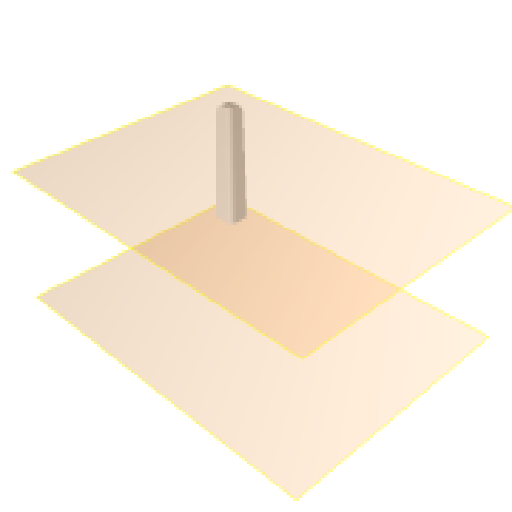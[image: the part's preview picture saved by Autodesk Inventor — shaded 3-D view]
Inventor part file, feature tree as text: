
AUTODESK INVENTOR PART (.ipt)
format: ipt  version: 2024.1 (Build 281209000, 209)  size: 171,008 bytes
history: native  units: mm
features: reference x4, sketch x3, plane x2, other x2, loft x1, extrude x1, fillet x1
ambient origin geometry x8: Origin, YZ Plane, XZ Plane, XY Plane, X Axis, Y Axis, Z Axis, Center Point
bodies: Body1 (feature_tree)
feature tree (14):
  plane  "Arbeitsebene1"
  sketch  "Skizze1"  dims[d0=10.0mm d1=2.0mm]
  plane  "Arbeitsebene2"
  loft  "Erhebung1"
  extrude  "Extrusion4"  TaperAngle=0.0deg  [1 undecoded]
  fillet  "Rundung1"  [1 undecoded]
  reference  "Referenz1"
  sketch  "Skizze4"  dims[d8=4.0mm d9=0.0mm d10=90.0deg d11=0.0mm d12=90.0deg]
  sketch  "Skizze5"  dims[d13=60.0mm d14=0.0mm d15=8.0mm d16=105.7mm]
  reference  "Referenz2"
  reference  "Referenz3"
  reference  "Referenz4"
  other  "Assembly_Planktoscope_Uc2version_wormdrive_V3.iam"
  other  "60_Planktoscope_MicroscopeHolder_Bottom_v0:1"
note: 2 required parameter values undecoded (feature->parameter linkage not recoverable at this tier; creation-order binding heuristic only, values carry confidence <= 0.55)
